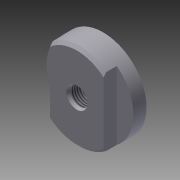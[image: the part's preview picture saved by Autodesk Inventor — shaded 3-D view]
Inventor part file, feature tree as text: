
AUTODESK INVENTOR PART (.ipt)
format: ipt  version: 2011 (Build 150239000, 239)  size: 93,696 bytes
history: native  units: in
note: dims shown in document units (in); Inventor stores cm internally (conversion verified against a paired STEP export)
features: extrude x2, sketch x2, hole x1, chamfer x1
ambient origin geometry x8: Origin, YZ Plane, XZ Plane, XY Plane, X Axis, Y Axis, Z Axis, Center Point
bodies: Solid1 (feature_tree)
feature tree (6):
  extrude  "Extrusion1"  Depth=0.312in TaperAngle=0.0deg
  extrude  "Extrusion2"  Depth=0.312in TaperAngle=0.0deg
  hole  "Hole1"  [1 undecoded]
  chamfer  "Chamfer1"  Distance=0.0625in Angle=45.0deg
  sketch  "Sketch1"  dims[d0=2.062in d1=0.312in d2=0.0in]
  sketch  "Sketch2"  dims[d5=1.272in d6=0.312in d7=0.0in d8=1.0in d9=1.0in d10=0.422in d11=0.395in d12=0.0246in d13=0.423in d14=0.5in d15=0.25in d16=45.0deg d17=0.75in d18=0.8108in d19=0.0625in d20=0.125in d21=45.0deg]
note: 1 required parameter value undecoded (feature->parameter linkage not recoverable at this tier; creation-order binding heuristic only, values carry confidence <= 0.55)
